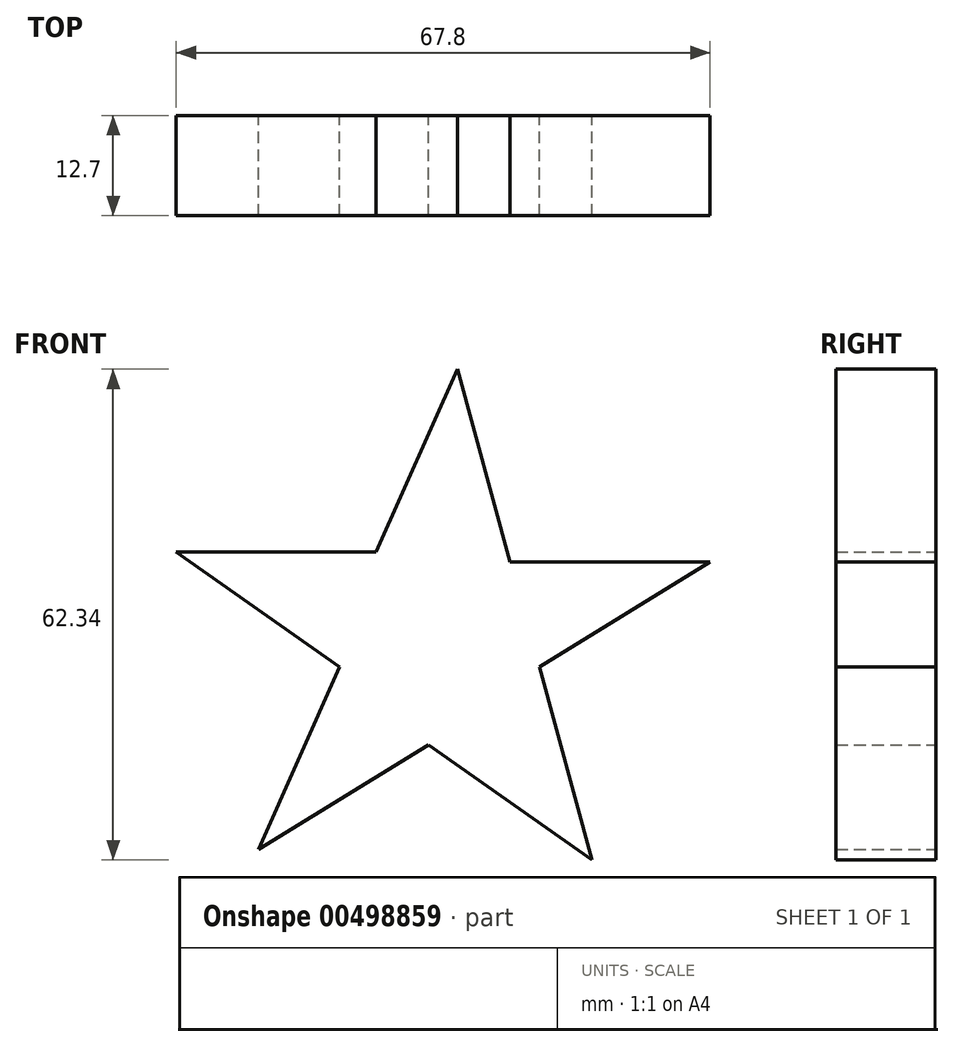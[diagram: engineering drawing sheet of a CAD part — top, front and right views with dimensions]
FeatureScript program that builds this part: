
annotation { "Feature Type Name" : "Feature", "Feature Type Description" : "" }
export const myFeature = defineFeature(function(context is Context, id is Id, definition is map)
    precondition{}
    {
        {
            var Q0;
            Q0=qCreatedBy(makeId("Front.planeOp"),FACE);
            var sketch = newSketch(context, id + "F0", { "sketchPlane" : qUnion([Q0])});
            skLineSegment(sketch, "E0", {"start": v(3.68, 0) * mm, "end": v(-6.66, -23.2) * mm});
            skLineSegment(sketch, "E1", {"start": v(-6.66, -23.2) * mm, "end": v(-32.06, -23.2) * mm});
            skLineSegment(sketch, "E2", {"start": v(-32.06, -23.2) * mm, "end": v(-11.3, -37.82) * mm});
            skLineSegment(sketch, "E3", {"start": v(-11.3, -37.82) * mm, "end": v(-21.63, -61.02) * mm});
            skLineSegment(sketch, "E4", {"start": v(-21.63, -61.02) * mm, "end": v(0, -47.71) * mm});
            skLineSegment(sketch, "E5", {"start": v(0, -47.71) * mm, "end": v(20.77, -62.34) * mm});
            skLineSegment(sketch, "E6", {"start": v(20.77, -62.34) * mm, "end": v(14.1, -37.82) * mm});
            skLineSegment(sketch, "E7", {"start": v(14.1, -37.82) * mm, "end": v(35.74, -24.51) * mm});
            skLineSegment(sketch, "E8", {"start": v(35.74, -24.51) * mm, "end": v(10.34, -24.51) * mm});
            skLineSegment(sketch, "E9", {"start": v(10.34, -24.51) * mm, "end": v(3.68, 0) * mm});
            skSolve(sketch);
        }
        {
            var Q0;
            Q0=makeQuery(id+"F0.imprint","IMPRINT",FACE,{"disambiguationData":[TD([[makeQuery(id+"F0.imprint","IMPRINT",EDGE,{"derivedFrom":sQuery(id+"F0.wireOp",EDGE,"E0")}),1.0]])]});
            extrude(context, id + "F1", {"entities" : qUnion([Q0]), "depth" : 12.7 * mm, "offsetDistance" : 25.4 * mm});
        }
    });
